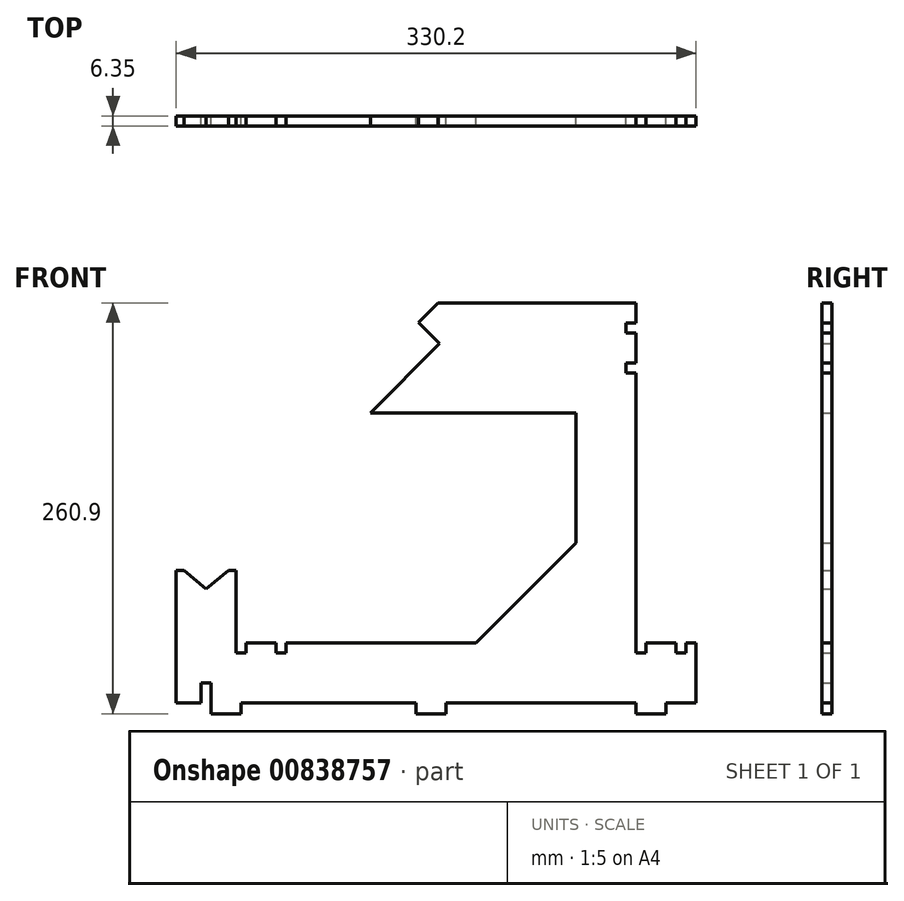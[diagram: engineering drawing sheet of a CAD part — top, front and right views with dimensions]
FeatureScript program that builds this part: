
annotation { "Feature Type Name" : "Feature", "Feature Type Description" : "" }
export const myFeature = defineFeature(function(context is Context, id is Id, definition is map)
    precondition{}
    {
        {
            var Q0;
            Q0=qCreatedBy(makeId("Front.planeOp"),FACE);
            var sketch = newSketch(context, id + "F0", { "sketchPlane" : qUnion([Q0])});
            skLineSegment(sketch, "E0", {"start": v(-82.64, -105.94) * mm, "end": v(-146.14, -169.44) * mm});
            skLineSegment(sketch, "E1", {"start": v(-146.14, -169.44) * mm, "end": v(-266.8, -169.44) * mm});
            skLineSegment(sketch, "E2", {"start": v(-336.64, -207.54) * mm, "end": v(-336.64, -123.4) * mm});
            skCircle(sketch, "E3", {"center": v(-317.6, -118.64) * mm, "radius": 12.7 * mm, "construction": true});
            skLineSegment(sketch, "E4.0", {"start": v(-336.64, -123.4) * mm, "end": v(-331.67, -123.4) * mm});
            skLineSegment(sketch, "E5", {"start": v(-298.54, -123.4) * mm, "end": v(-298.54, -175.79) * mm});
            skLineSegment(sketch, "E6.trimOffspring", {"start": v(-303.5, -123.4) * mm, "end": v(-298.54, -123.4) * mm});
            skPoint(sketch, "E7.orphan", {"position": v(-317.6, -130.6) * mm});
            skLineSegment(sketch, "E8.0", {"start": v(-331.67, -123.4) * mm, "end": v(-317.6, -135.21) * mm});
            skLineSegment(sketch, "E9.0", {"start": v(-303.5, -123.4) * mm, "end": v(-317.6, -135.21) * mm});
            skLineSegment(sketch, "E10", {"start": v(-325.75, -128.36) * mm, "end": v(-317.6, -118.64) * mm, "construction": true});
            skLineSegment(sketch, "E11", {"start": v(-309.43, -128.36) * mm, "end": v(-317.6, -118.64) * mm, "construction": true});
            skLineSegment(sketch, "E12.0", {"start": v(-6.44, -207.54) * mm, "end": v(-314.42, -207.54) * mm});
            skLineSegment(sketch, "E13", {"start": v(-44.54, 46.46) * mm, "end": v(-44.54, 33.76) * mm});
            skLineSegment(sketch, "E14", {"start": v(-38.2, -169.44) * mm, "end": v(-19.14, -169.44) * mm});
            skLineSegment(sketch, "E15", {"start": v(-6.44, -169.44) * mm, "end": v(-6.44, -207.54) * mm});
            skLineSegment(sketch, "E16", {"start": v(-82.64, -105.94) * mm, "end": v(-82.64, -23.39) * mm});
            skLineSegment(sketch, "E17", {"start": v(-231.32, -23.39) * mm, "end": v(-213.36, -23.39) * mm, "construction": true});
            skLineSegment(sketch, "E18.0", {"start": v(-170.45, 46.46) * mm, "end": v(-44.54, 46.46) * mm});
            skLineSegment(sketch, "E19.top", {"start": v(-320.77, -194.84) * mm, "end": v(-314.42, -194.84) * mm});
            skLineSegment(sketch, "E19.left", {"start": v(-320.77, -207.54) * mm, "end": v(-320.77, -194.84) * mm});
            skLineSegment(sketch, "E19.right", {"start": v(-314.42, -207.54) * mm, "end": v(-314.42, -194.84) * mm});
            skLineSegment(sketch, "E20.trimOffspring", {"start": v(-320.77, -207.54) * mm, "end": v(-336.64, -207.54) * mm});
            skLineSegment(sketch, "E21.top", {"start": v(-298.54, -175.79) * mm, "end": v(-292.2, -175.79) * mm});
            skLineSegment(sketch, "E21.right", {"start": v(-292.2, -169.44) * mm, "end": v(-292.2, -175.79) * mm});
            skLineSegment(sketch, "E22.bottom", {"start": v(-273.14, -175.79) * mm, "end": v(-266.8, -175.79) * mm});
            skLineSegment(sketch, "E22.left", {"start": v(-273.14, -175.79) * mm, "end": v(-273.14, -169.44) * mm});
            skLineSegment(sketch, "E22.right", {"start": v(-266.8, -175.79) * mm, "end": v(-266.8, -169.44) * mm});
            skLineSegment(sketch, "E23.trimOffspring", {"start": v(-273.14, -169.44) * mm, "end": v(-292.2, -169.44) * mm});
            skLineSegment(sketch, "E24.top", {"start": v(-44.54, -175.79) * mm, "end": v(-38.2, -175.79) * mm});
            skLineSegment(sketch, "E24.right", {"start": v(-38.2, -169.44) * mm, "end": v(-38.2, -175.79) * mm});
            skLineSegment(sketch, "E25.bottom", {"start": v(-19.14, -175.79) * mm, "end": v(-12.8, -175.79) * mm});
            skLineSegment(sketch, "E25.left", {"start": v(-19.14, -175.79) * mm, "end": v(-19.14, -169.44) * mm});
            skLineSegment(sketch, "E25.right", {"start": v(-12.8, -175.79) * mm, "end": v(-12.8, -169.44) * mm});
            skLineSegment(sketch, "E26.trimOffspring", {"start": v(-12.8, -169.44) * mm, "end": v(-6.44, -169.44) * mm});
            skLineSegment(sketch, "E27.bottom", {"start": v(-44.54, 33.76) * mm, "end": v(-50.9, 33.76) * mm});
            skLineSegment(sketch, "E27.top", {"start": v(-44.54, 27.41) * mm, "end": v(-50.9, 27.41) * mm});
            skLineSegment(sketch, "E27.right", {"start": v(-50.9, 33.76) * mm, "end": v(-50.9, 27.41) * mm});
            skLineSegment(sketch, "E28.bottom", {"start": v(-50.9, 8.36) * mm, "end": v(-44.54, 8.36) * mm});
            skLineSegment(sketch, "E28.top", {"start": v(-50.9, 2.01) * mm, "end": v(-44.54, 2.01) * mm});
            skLineSegment(sketch, "E28.left", {"start": v(-50.9, 8.36) * mm, "end": v(-50.9, 2.01) * mm});
            skLineSegment(sketch, "E29.trimOffspring", {"start": v(-44.54, 27.41) * mm, "end": v(-44.54, 8.36) * mm});
            skLineSegment(sketch, "E30.trimOffspring", {"start": v(-44.54, 2.01) * mm, "end": v(-44.54, -175.79) * mm});
            skLineSegment(sketch, "E31", {"start": v(-317.6, -118.64) * mm, "end": v(-298.07, -99.11) * mm, "construction": true});
            skLineSegment(sketch, "E32.0", {"start": v(-326.57, -109.66) * mm, "end": v(-182.89, 34.03) * mm, "construction": true});
            skLineSegment(sketch, "E33", {"start": v(-182.89, 34.03) * mm, "end": v(-169.42, 20.56) * mm});
            skLineSegment(sketch, "E34", {"start": v(-182.89, 34.03) * mm, "end": v(-170.45, 46.46) * mm});
            skLineSegment(sketch, "E35.trimOffspring", {"start": v(-231.32, -23.39) * mm, "end": v(-178.4, 29.54) * mm, "construction": true});
            skLineSegment(sketch, "E36.bottom", {"start": v(-25.5, -207.54) * mm, "end": v(-44.54, -207.54) * mm});
            skLineSegment(sketch, "E36.top", {"start": v(-25.5, -214.44) * mm, "end": v(-44.54, -214.44) * mm});
            skLineSegment(sketch, "E36.left", {"start": v(-25.5, -207.54) * mm, "end": v(-25.5, -214.44) * mm});
            skLineSegment(sketch, "E36.right", {"start": v(-44.54, -207.54) * mm, "end": v(-44.54, -214.44) * mm});
            skLineSegment(sketch, "E37.bottom", {"start": v(-165.2, -207.54) * mm, "end": v(-184.24, -207.54) * mm});
            skLineSegment(sketch, "E37.top", {"start": v(-165.2, -214.44) * mm, "end": v(-184.24, -214.44) * mm});
            skLineSegment(sketch, "E37.left", {"start": v(-165.2, -207.54) * mm, "end": v(-165.2, -214.44) * mm});
            skLineSegment(sketch, "E37.right", {"start": v(-184.24, -207.54) * mm, "end": v(-184.24, -214.44) * mm});
            skLineSegment(sketch, "E38.bottom", {"start": v(-295.37, -207.54) * mm, "end": v(-314.42, -207.54) * mm});
            skLineSegment(sketch, "E38.top", {"start": v(-295.37, -214.44) * mm, "end": v(-314.42, -214.44) * mm});
            skLineSegment(sketch, "E38.left", {"start": v(-295.37, -207.54) * mm, "end": v(-295.37, -214.44) * mm});
            skLineSegment(sketch, "E38.right", {"start": v(-314.42, -207.54) * mm, "end": v(-314.42, -214.44) * mm});
            skLineSegment(sketch, "E39.0", {"start": v(-213.36, -23.39) * mm, "end": v(-169.42, 20.56) * mm});
            skLineSegment(sketch, "E40", {"start": v(-213.36, -23.39) * mm, "end": v(-82.64, -23.39) * mm});
            skSolve(sketch);
        }
        {
            var Q0;
            Q0=qSketchRegion(id+"F0",true);
            extrude(context, id + "F1", {"entities" : qUnion([Q0]), "depth" : 6.35 * mm, "offsetDistance" : 25.4 * mm});
        }
    });
